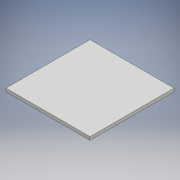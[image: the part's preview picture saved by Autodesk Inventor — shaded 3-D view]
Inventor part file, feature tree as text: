
AUTODESK INVENTOR PART (.ipt)
format: ipt  version: 2018 (Build 220112000, 112)  size: 89,600 bytes
history: native  units: mm
features: other x1, extrude x1, sketch x1
ambient origin geometry x8: Origin, YZ Plane, XZ Plane, XY Plane, X Axis, Y Axis, Z Axis, Center Point
bodies: Body1 (feature_tree)
feature tree (3):
  other  "Bryła1"
  extrude  "Wyciągnięcie proste1"  Depth=156.0mm
  sketch  "Szkic1"
